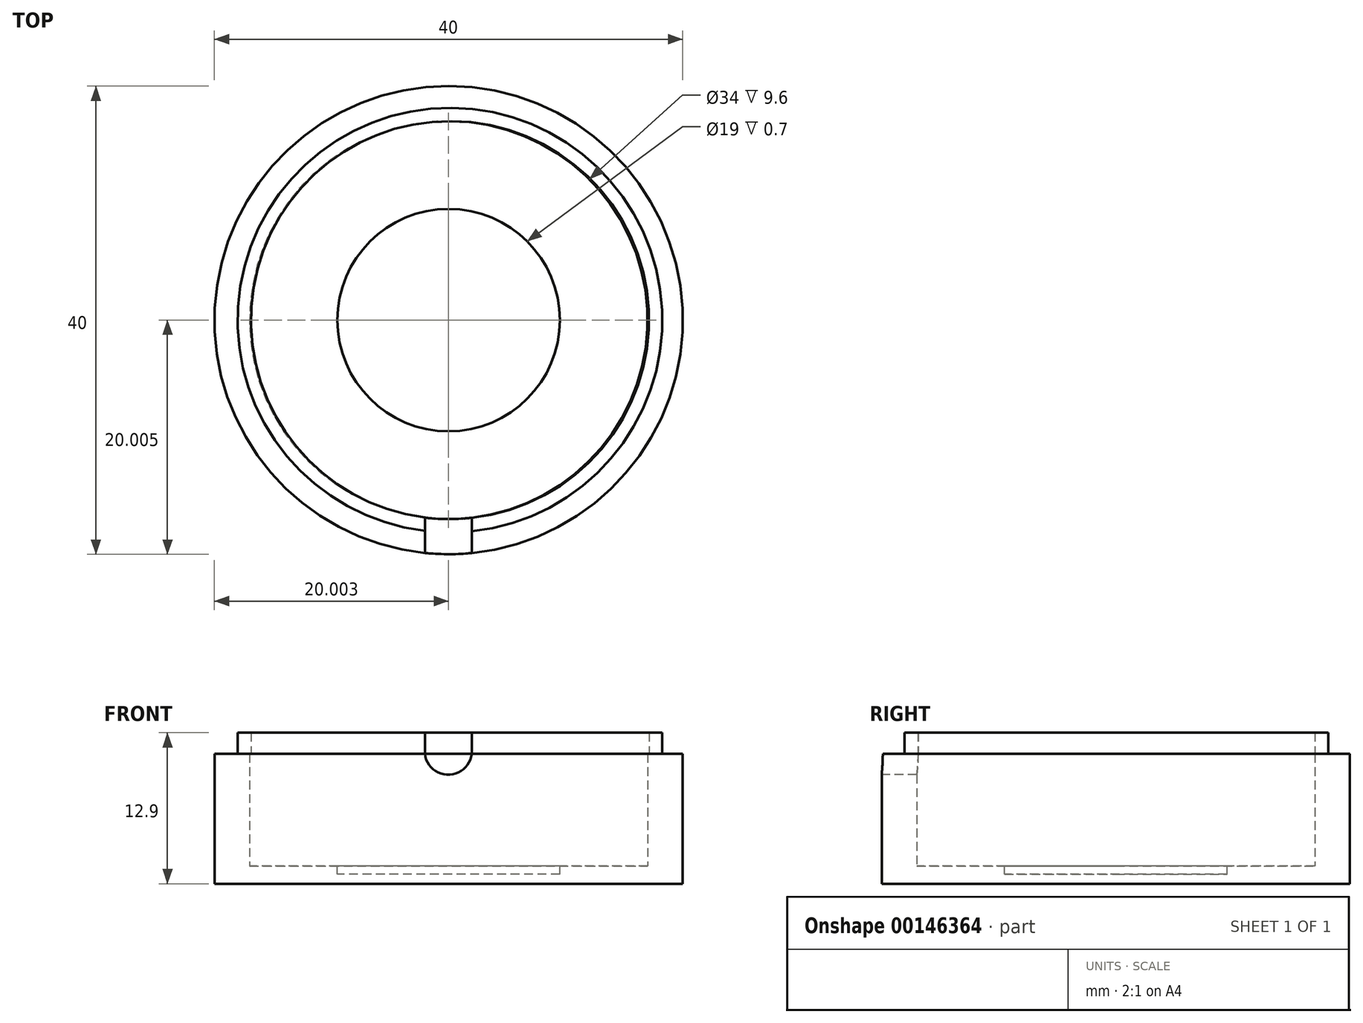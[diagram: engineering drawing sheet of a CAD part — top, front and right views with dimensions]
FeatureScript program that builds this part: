
annotation { "Feature Type Name" : "Feature", "Feature Type Description" : "" }
export const myFeature = defineFeature(function(context is Context, id is Id, definition is map)
    precondition{}
    {
        {
            var Q0;
            Q0=qCreatedBy(makeId("Top.planeOp"),FACE);
            var sketch = newSketch(context, id + "F0", { "sketchPlane" : qUnion([Q0])});
            skCircle(sketch, "E0", {"center": v(-50.79, 33.4) * mm, "radius": 20 * mm});
            skSolve(sketch);
        }
        {
            var Q0;
            Q0=makeQuery(id+"F0.imprint","IMPRINT",FACE,{"disambiguationData":[TD([[makeQuery(id+"F0.imprint","IMPRINT",EDGE,{"derivedFrom":sQuery(id+"F0.wireOp",EDGE,"E0")}),1.0]])]});
            extrude(context, id + "F1", {"entities" : qUnion([Q0]), "depth" : 1.5 * mm});
        }
        {
            var Q0;
            Q0=makeQuery(id+"F1.opExtrude","CAP_FACE",FACE,{"disambiguationData":[OSD([sQuery(id+"F0.wireOp",EDGE,"E0"),sQuery(id+"F0.wireOp",EDGE,"IqYGBItP-6JEx-q2S6-xiGm-nLTTzCfwcT9q")])],"isStart":false});
            var sketch = newSketch(context, id + "F2", { "sketchPlane" : qUnion([Q0])});
            skCircle(sketch, "E1", {"center": v(-50.79, 33.4) * mm, "radius": 17 * mm});
            skSolve(sketch);
        }
        {
            var Q0;
            Q0=makeQuery(id+"F2.imprint","IMPRINT",FACE,{"disambiguationData":[TD([[makeQuery(id+"F2.imprint","IMPRINT",EDGE,{"derivedFrom":sQuery(id+"F2.wireOp",EDGE,"E1")}),-1.0]])]});
            extrude(context, id + "F3", {"entities" : qUnion([Q0]), "operationType" : NewBodyOperationType.ADD, "depth" : 9.6 * mm});
        }
        {
            var Q0;
            Q0=makeQuery(id+"F3.opExtrude","CAP_FACE",FACE,{"disambiguationData":[OSD([sQuery(id+"F0.wireOp",EDGE,"E0"),sQuery(id+"F2.wireOp",EDGE,"E1")])],"isStart":false});
            var sketch = newSketch(context, id + "F4", { "sketchPlane" : qUnion([Q0])});
            skLineSegment(sketch, "E2", {"start": v(-50.67, 50.4) * mm, "end": v(-50.67, 16.4) * mm, "construction": true});
            skCircle(sketch, "E3", {"center": v(-50.67, 33.4) * mm, "radius": 18.14 * mm});
            skLineSegment(sketch, "E4", {"start": v(-50.67, 33.4) * mm, "end": v(-25.06, 33.4) * mm, "construction": true});
            skLineSegment(sketch, "E5", {"start": v(-33.79, 33.4) * mm, "end": v(-32.54, 33.4) * mm, "construction": true});
            skCircle(sketch, "E6", {"center": v(-50.67, 33.4) * mm, "radius": 17 * mm});
            skSolve(sketch);
        }
        {
            var Q0;
            Q0=qSketchRegion(id+"F4",true);
            extrude(context, id + "F5", {"entities" : qUnion([Q0]), "operationType" : NewBodyOperationType.ADD, "depth" : 1.8 * mm});
        }
        {
            var Q0;
            Q0=qCreatedBy(makeId("Front.planeOp"),FACE);
            var sketch = newSketch(context, id + "F6", { "sketchPlane" : qUnion([Q0])});
            skLineSegment(sketch, "E7", {"start": v(-70.82, 9.31) * mm, "end": v(-30.82, 9.31) * mm, "construction": true});
            skLineSegment(sketch, "E8", {"start": v(-30.82, 11.11) * mm, "end": v(-30.82, 8.32) * mm, "construction": true});
            skLineSegment(sketch, "E9", {"start": v(-70.82, 9.44) * mm, "end": v(-70.82, 9.24) * mm, "construction": true});
            skPoint(sketch, "E10.end.orphan", {"position": v(-50.83, 0) * mm});
            skLineSegment(sketch, "E11", {"start": v(-50.82, 9.31) * mm, "end": v(-50.82, 17.42) * mm, "construction": true});
            skLineSegment(sketch, "E12", {"start": v(-52.82, 17.42) * mm, "end": v(-52.82, 11.1) * mm});
            skLineSegment(sketch, "E13.MirrorCS", {"start": v(-48.82, 17.42) * mm, "end": v(-48.82, 11.1) * mm});
            skArc(sketch, "E14", {"start": v(-52.82, 11.1) * mm, "mid": v(-50.82, 9.31) * mm, "end": v(-48.82, 11.1) * mm});
            skLineSegment(sketch, "E15", {"start": v(-52.82, 17.42) * mm, "end": v(-48.82, 17.42) * mm});
            skSolve(sketch);
        }
        {
            var Q0;
            Q0=makeQuery(id+"F6.imprint","IMPRINT",FACE,{"disambiguationData":[TD([[makeQuery(id+"F6.imprint","IMPRINT",EDGE,{"derivedFrom":sQuery(id+"F6.wireOp",EDGE,"E12")}),1.0]])]});
            var Q1;
            Q1=sQuery(id+"F6.wireOp",EDGE,"E15");
            var Q2;
            Q2=sQuery(id+"F6.wireOp",EDGE,"E12");
            var Q3;
            Q3=sQuery(id+"F6.wireOp",EDGE,"E13.MirrorCS");
            var Q4;
            Q4=sQuery(id+"F6.wireOp",EDGE,"E14");
            extrude(context, id + "F7", {"entities" : qUnion([Q0]), "operationType" : NewBodyOperationType.REMOVE, "surfaceEntities" : qUnion([Q1, Q2, Q3, Q4]), "oppositeDirection" : true, "depth" : 20 * mm});
        }
        {
            var Q0;
            Q0=makeQuery(id+"F1.opExtrude","CAP_FACE",FACE,{"disambiguationData":[OSD([sQuery(id+"F0.wireOp",EDGE,"E0")])],"isStart":false});
            var sketch = newSketch(context, id + "F8", { "sketchPlane" : qUnion([Q0])});
            skCircle(sketch, "E16", {"center": v(-50.79, 33.4) * mm, "radius": 9.5 * mm});
            skSolve(sketch);
        }
        {
            var Q0;
            Q0=makeQuery(id+"F8.imprint","IMPRINT",FACE,{"disambiguationData":[TD([[makeQuery(id+"F8.imprint","IMPRINT",EDGE,{"derivedFrom":sQuery(id+"F8.wireOp",EDGE,"E16")}),1.0]])]});
            extrude(context, id + "F9", {"entities" : qUnion([Q0]), "operationType" : NewBodyOperationType.REMOVE, "oppositeDirection" : true, "depth" : 0.7 * mm});
        }
    });
